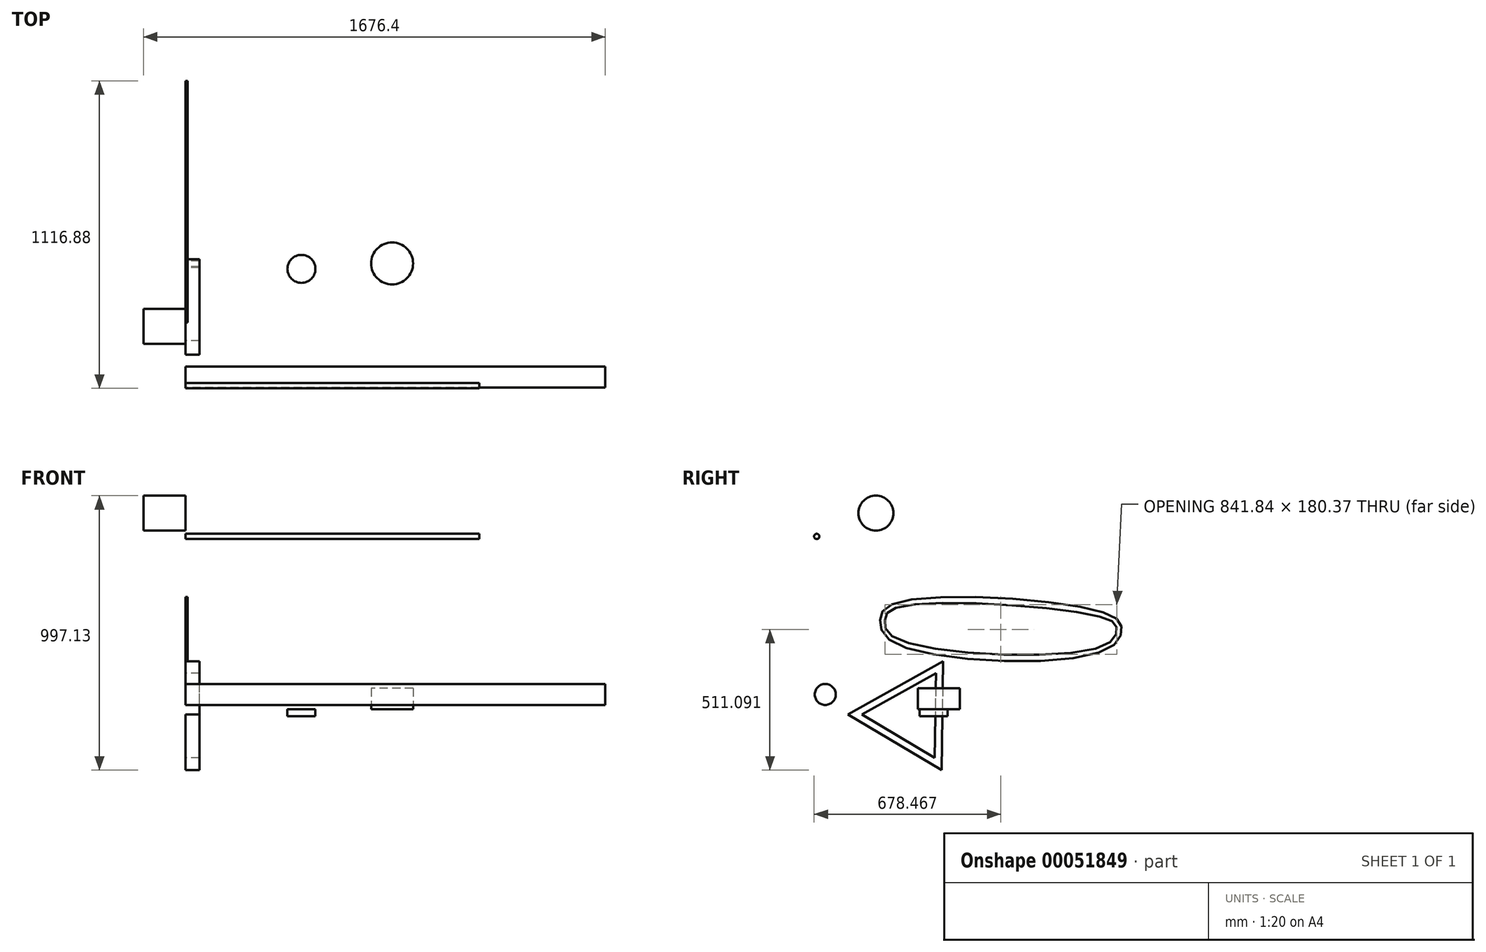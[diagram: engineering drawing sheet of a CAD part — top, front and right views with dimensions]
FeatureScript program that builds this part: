
annotation { "Feature Type Name" : "Feature", "Feature Type Description" : "" }
export const myFeature = defineFeature(function(context is Context, id is Id, definition is map)
    precondition{}
    {
        {
            var Q0;
            Q0=qCreatedBy(makeId("Right.planeOp"),FACE);
            var sketch = newSketch(context, id + "F0", { "sketchPlane" : qUnion([Q0])});
            skCircle(sketch, "E0.cCircle", {"center": v(-1.36, 3.4) * mm, "radius": 228.6 * mm, "construction": true});
            skLineSegment(sketch, "E0.0", {"start": v(-229.94, 6.64) * mm, "end": v(115.74, 199.73) * mm});
            skLineSegment(sketch, "E0.1", {"start": v(115.74, 199.73) * mm, "end": v(110.12, -196.17) * mm});
            skLineSegment(sketch, "E0.2", {"start": v(110.12, -196.17) * mm, "end": v(-229.94, 6.64) * mm});
            skCircle(sketch, "E1.cCircle", {"center": v(-1.36, 3.4) * mm, "radius": 177.8 * mm, "construction": true});
            skLineSegment(sketch, "E1.0", {"start": v(85.35, -151.82) * mm, "end": v(-179.14, 5.92) * mm});
            skLineSegment(sketch, "E1.1", {"start": v(-179.14, 5.92) * mm, "end": v(89.72, 156.1) * mm});
            skLineSegment(sketch, "E1.2", {"start": v(89.72, 156.1) * mm, "end": v(85.35, -151.82) * mm});
            skSolve(sketch);
        }
        {
            var Q0;
            Q0=makeQuery(id+"F0.imprint","IMPRINT",FACE,{"disambiguationData":[TD([[makeQuery(id+"F0.imprint","IMPRINT",EDGE,{"derivedFrom":sQuery(id+"F0.wireOp",EDGE,"E0.0")}),-1.0]])]});
            extrude(context, id + "F1", {"entities" : qUnion([Q0]), "depth" : 50.8 * mm});
        }
        {
            var Q0;
            Q0=qCreatedBy(makeId("Right.planeOp"),FACE);
            var sketch = newSketch(context, id + "F2", { "sketchPlane" : qUnion([Q0])});
            skCircle(sketch, "E2", {"center": v(-312.06, 78.91) * mm, "radius": 38.1 * mm});
            skSolve(sketch);
        }
        {
            var Q0;
            Q0 = qSketchRegion(id + "F2", true);
            extrude(context, id + "F3", {"entities" : qUnion([Q0]), "depth" : 1524 * mm});
        }
        {
            var Q0;
            Q0=qCreatedBy(makeId("Top.planeOp"),FACE);
            var sketch = newSketch(context, id + "F4", { "sketchPlane" : qUnion([Q0])});
            skCircle(sketch, "E3", {"center": v(420.8, 81.16) * mm, "radius": 50.8 * mm});
            skSolve(sketch);
        }
        {
            var Q0;
            Q0 = qSketchRegion(id + "F4", true);
            extrude(context, id + "F5", {"entities" : qUnion([Q0]), "depth" : 25.4 * mm});
        }
        {
            var Q0;
            Q0=makeQuery(id+"F5.opExtrude","CAP_FACE",FACE,{"disambiguationData":[OSD([sQuery(id+"F4.wireOp",EDGE,"E3")])],"isStart":false});
            var sketch = newSketch(context, id + "F6", { "sketchPlane" : qUnion([Q0])});
            skCircle(sketch, "E4", {"center": v(750.1, 101) * mm, "radius": 76.2 * mm});
            skSolve(sketch);
        }
        {
            var Q0;
            Q0 = qSketchRegion(id + "F6", true);
            extrude(context, id + "F7", {"entities" : qUnion([Q0]), "depth" : 76.2 * mm});
        }
        {
            var Q0;
            Q0=qCreatedBy(makeId("Right.planeOp"),FACE);
            var sketch = newSketch(context, id + "F8", { "sketchPlane" : qUnion([Q0])});
            skFitSpline(sketch, "E5", {"points": [v(-95.04, 348.67) * mm, v(-61.52, 285.15) * mm, v(688.37, 251.63) * mm, v(746.6, 316.91) * mm, v(688.37, 361.02) * mm, v(-54.46, 394.55) * mm, v(-95.04, 348.67) * mm]});
            skFitSpline(sketch, "E6", {"points": [v(-113.23, 348.67) * mm, v(-54.46, 412.36) * mm, v(693.32, 378.56) * mm, v(764.2, 316.91) * mm, v(691.24, 234.17) * mm, v(-54.46, 262.45) * mm, v(-113.23, 348.67) * mm]});
            skSolve(sketch);
        }
        {
            var Q0;
            Q0 = qSketchRegion(id + "F8", true);
            extrude(context, id + "F9", {"entities" : qUnion([Q0]), "depth" : 7.62 * mm});
        }
        {
            var Q0;
            Q0=makeQuery(id+"F8.imprint","IMPRINT",FACE,{"disambiguationData":[TD([[makeQuery(id+"F8.imprint","IMPRINT",EDGE,{"derivedFrom":sQuery(id+"F8.wireOp",EDGE,"E5")}),1.0]])]});
            var sketch = newSketch(context, id + "F10", { "sketchPlane" : qUnion([Q0])});
            skCircle(sketch, "E7", {"center": v(-128.08, 737.46) * mm, "radius": 63.5 * mm});
            skSolve(sketch);
        }
        {
            var Q0;
            Q0=makeQuery(id+"F10.imprint","IMPRINT",FACE,{"disambiguationData":[TD([[makeQuery(id+"F10.imprint","IMPRINT",EDGE,{"derivedFrom":sQuery(id+"F10.wireOp",EDGE,"E7")}),1.0]])]});
            var Q1;
            Q1=sQuery(id+"F10.wireOp",EDGE,"E7");
            extrude(context, id + "F11", {"entities" : qUnion([Q0]), "surfaceEntities" : qUnion([Q1]), "oppositeDirection" : true, "depth" : 152.4 * mm});
        }
        {
            var Q0;
            Q0=makeQuery(id+"F8.imprint","IMPRINT",FACE,{"disambiguationData":[TD([[makeQuery(id+"F8.imprint","IMPRINT",EDGE,{"derivedFrom":sQuery(id+"F8.wireOp",EDGE,"E5")}),1.0]])]});
            var sketch = newSketch(context, id + "F12", { "sketchPlane" : qUnion([Q0])});
            skCircle(sketch, "E8", {"center": v(-343.06, 652.85) * mm, "radius": 9.52 * mm});
            skSolve(sketch);
        }
        {
            var Q0;
            Q0=makeQuery(id+"F12.imprint","IMPRINT",FACE,{"disambiguationData":[TD([[makeQuery(id+"F12.imprint","IMPRINT",EDGE,{"derivedFrom":sQuery(id+"F12.wireOp",EDGE,"E8")}),1.0]])]});
            extrude(context, id + "F13", {"entities" : qUnion([Q0]), "depth" : 1066.8 * mm});
        }
    });
